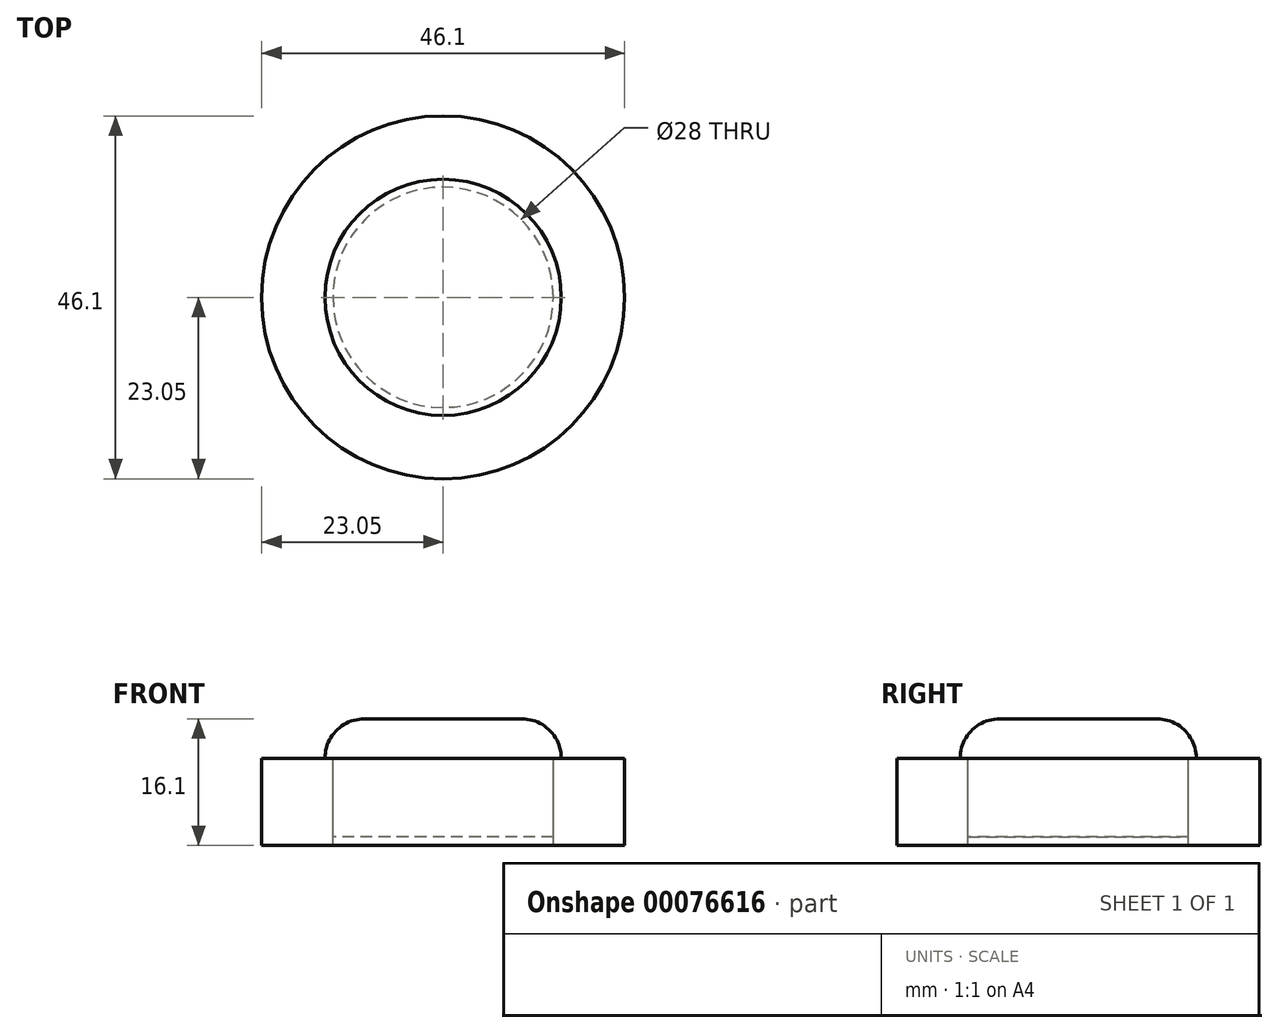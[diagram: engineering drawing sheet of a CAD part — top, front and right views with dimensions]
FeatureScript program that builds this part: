
annotation { "Feature Type Name" : "Feature", "Feature Type Description" : "" }
export const myFeature = defineFeature(function(context is Context, id is Id, definition is map)
    precondition{}
    {
        {
            var Q0;
            Q0=qCreatedBy(makeId("Top.planeOp"),FACE);
            var sketch = newSketch(context, id + "F0", { "sketchPlane" : qUnion([Q0])});
            skCircle(sketch, "E0", {"center": v(0, 0) * mm, "radius": 23.05 * mm});
            skCircle(sketch, "E1", {"center": v(0, 0) * mm, "radius": 15 * mm});
            skCircle(sketch, "E2", {"center": v(0, 0) * mm, "radius": 14 * mm});
            skSolve(sketch);
        }
        {
            var Q0;
            Q0=makeQuery(id+"F0.imprint","IMPRINT",FACE,{"disambiguationData":[TD([[makeQuery(id+"F0.imprint","IMPRINT",EDGE,{"derivedFrom":sQuery(id+"F0.wireOp",EDGE,"E2")}),1.0]])]});
            var Q1;
            Q1=makeQuery(id+"F0.imprint","IMPRINT",FACE,{"disambiguationData":[TD([[makeQuery(id+"F0.imprint","IMPRINT",EDGE,{"derivedFrom":sQuery(id+"F0.wireOp",EDGE,"E1")}),1.0]])]});
            extrude(context, id + "F1", {"entities" : qUnion([Q0, Q1]), "depth" : 5 * mm});
        }
        {
            var Q0;
            Q0=makeQuery(id+"F0.imprint","IMPRINT",FACE,{"disambiguationData":[TD([[makeQuery(id+"F0.imprint","IMPRINT",EDGE,{"derivedFrom":sQuery(id+"F0.wireOp",EDGE,"E2")}),1.0]])]});
            extrude(context, id + "F2", {"entities" : qUnion([Q0]), "oppositeDirection" : true, "depth" : 10 * mm});
        }
        {
            var Q0;
            Q0=makeQuery(id+"F0.imprint","IMPRINT",FACE,{"disambiguationData":[TD([[makeQuery(id+"F0.imprint","IMPRINT",EDGE,{"derivedFrom":sQuery(id+"F0.wireOp",EDGE,"E0")}),1.0]])]});
            var Q1;
            Q1=makeQuery(id+"F0.imprint","IMPRINT",FACE,{"disambiguationData":[TD([[makeQuery(id+"F0.imprint","IMPRINT",EDGE,{"derivedFrom":sQuery(id+"F0.wireOp",EDGE,"E1")}),1.0]])]});
            extrude(context, id + "F3", {"entities" : qUnion([Q0, Q1]), "oppositeDirection" : true, "depth" : 11.1 * mm});
        }
        {
            var Q0;
            Q0=makeQuery(id+"F1.opExtrude","CAP_EDGE",EDGE,{"disambiguationData":[OSD([sQuery(id+"F0.wireOp",EDGE,"E1")])],"isStart":false});
            fillet(context, id + "F4", {"entities" : qUnion([Q0]), "radius" : 5 * mm, "tangentPropagation" : true, "allowEdgeOverflow" : false});
        }
    });
